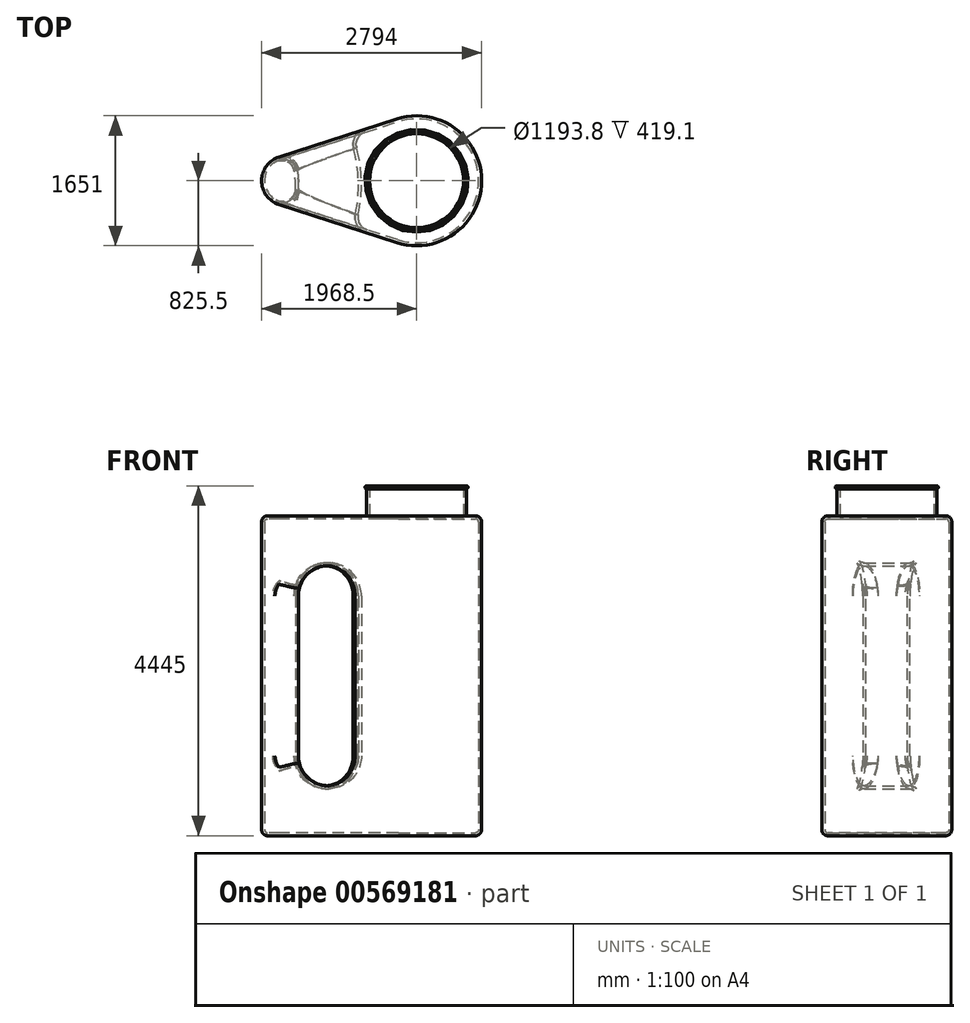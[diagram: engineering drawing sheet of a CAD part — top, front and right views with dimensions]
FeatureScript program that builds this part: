
annotation { "Feature Type Name" : "Feature", "Feature Type Description" : "" }
export const myFeature = defineFeature(function(context is Context, id is Id, definition is map)
    precondition{}
    {
        {
            var Q0;
            Q0=qCreatedBy(makeId("Top.planeOp"),FACE);
            var sketch = newSketch(context, id + "F0", { "sketchPlane" : qUnion([Q0])});
            skArc(sketch, "E0", {"start": v(-254, -785.45) * mm, "mid": v(825.5, 0) * mm, "end": v(-254, 785.45) * mm});
            skLineSegment(sketch, "E1", {"start": v(-254, 785.45) * mm, "end": v(-1748.7, 302.1) * mm});
            skLineSegment(sketch, "E2", {"start": v(-1748.7, -302.1) * mm, "end": v(-254, -785.45) * mm});
            skArc(sketch, "E3", {"start": v(-1748.7, 302.1) * mm, "mid": v(-1968.5, 0) * mm, "end": v(-1748.7, -302.1) * mm});
            skSolve(sketch);
        }
        {
            var Q0;
            Q0=makeQuery(id+"F0.imprint","IMPRINT",FACE,{"disambiguationData":[TD([[makeQuery(id+"F0.imprint","IMPRINT",EDGE,{"derivedFrom":sQuery(id+"F0.wireOp",EDGE,"E0")}),1.0]])]});
            extrude(context, id + "F1", {"entities" : qUnion([Q0]), "depth" : 4064 * mm, "offsetDistance" : 25.4 * mm});
        }
        {
            var Q0;
            Q0=makeQuery(id+"F1.opExtrude","SWEPT_FACE",FACE,{"disambiguationData":[OSD([sQuery(id+"F0.wireOp",EDGE,"E2")])]});
            var sketch = newSketch(context, id + "F2", { "sketchPlane" : qUnion([Q0])});
            skArc(sketch, "E4", {"start": v(-600.09, 3048) * mm, "mid": v(-981.09, 3429) * mm, "end": v(-1362.09, 3048) * mm});
            skArc(sketch, "E5", {"start": v(-1362.08, 1016) * mm, "mid": v(-981.08, 635) * mm, "end": v(-600.08, 1016) * mm});
            skLineSegment(sketch, "E6", {"start": v(-600.09, 3048) * mm, "end": v(-600.08, 1016) * mm});
            skLineSegment(sketch, "E7", {"start": v(-1362.09, 3048) * mm, "end": v(-1362.08, 1016) * mm});
            skLineSegment(sketch, "E8", {"start": v(-2387.75, 4364.56) * mm, "end": v(-2387.75, -220.57) * mm, "construction": true});
            skLineSegment(sketch, "E9", {"start": v(283.93, 0) * mm, "end": v(283.93, 5172.73) * mm, "construction": true});
            skSolve(sketch);
        }
        {
            var Q0;
            Q0=makeQuery(id+"F2.imprint","IMPRINT",FACE,{"disambiguationData":[TD([[makeQuery(id+"F2.imprint","IMPRINT",EDGE,{"derivedFrom":sQuery(id+"F2.wireOp",EDGE,"E4")}),1.0]])]});
            var Q1;
            Q1=sQuery(id+"F2.wireOp",EDGE,"E8");
            revolve(context, id + "F3", {"operationType" : NewBodyOperationType.REMOVE, "entities" : qUnion([Q0]), "axis" : qUnion([Q1]), "revolveType" : RevolveType.FULL, "oppositeDirection" : true});
        }
        {
            var Q0;
            Q0=makeQuery(id+"F1.opExtrude","CAP_FACE",FACE,{"disambiguationData":[OSD([sQuery(id+"F0.wireOp",EDGE,"E0"),sQuery(id+"F0.wireOp",EDGE,"E1"),sQuery(id+"F0.wireOp",EDGE,"E2"),sQuery(id+"F0.wireOp",EDGE,"E3")])],"isStart":false});
            var sketch = newSketch(context, id + "F4", { "sketchPlane" : qUnion([Q0])});
            skCircle(sketch, "E10", {"center": v(0, 0) * mm, "radius": 635 * mm});
            skSolve(sketch);
        }
        {
            var Q0;
            Q0=makeQuery(id+"F4.imprint","IMPRINT",FACE,{"disambiguationData":[TD([[makeQuery(id+"F4.imprint","IMPRINT",EDGE,{"derivedFrom":sQuery(id+"F4.wireOp",EDGE,"E10")}),1.0]])]});
            extrude(context, id + "F5", {"entities" : qUnion([Q0]), "operationType" : NewBodyOperationType.ADD, "depth" : 381 * mm, "offsetDistance" : 25.4 * mm});
        }
        {
            var Q0;
            Q0=makeQuery(id+"F3.boolean.opBoolean","INTERSECT",EDGE,{"derivedFrom":[makeQuery(id+"F1.opExtrude","SWEPT_FACE",FACE,{"disambiguationData":[OSD([sQuery(id+"F0.wireOp",EDGE,"E2")])]}),makeQuery(id+"F3.opRevolve","SWEPT_FACE",FACE,{"disambiguationData":[OSD([sQuery(id+"F2.wireOp",EDGE,"E7")])]})]});
            var Q1;
            Q1=makeQuery(id+"F3.boolean.opBoolean","INTERSECT",EDGE,{"derivedFrom":[makeQuery(id+"F1.opExtrude","SWEPT_FACE",FACE,{"disambiguationData":[OSD([sQuery(id+"F0.wireOp",EDGE,"E2")])]}),makeQuery(id+"F3.opRevolve","SWEPT_FACE",FACE,{"disambiguationData":[OSD([sQuery(id+"F2.wireOp",EDGE,"E4")])]})]});
            var Q2;
            Q2=makeQuery(id+"F3.boolean.opBoolean","INTERSECT",EDGE,{"derivedFrom":[makeQuery(id+"F1.opExtrude","SWEPT_FACE",FACE,{"disambiguationData":[OSD([sQuery(id+"F0.wireOp",EDGE,"E2")])]}),makeQuery(id+"F3.opRevolve","SWEPT_FACE",FACE,{"disambiguationData":[OSD([sQuery(id+"F2.wireOp",EDGE,"E6")])]})]});
            var Q3;
            Q3=makeQuery(id+"F3.boolean.opBoolean","INTERSECT",EDGE,{"derivedFrom":[makeQuery(id+"F1.opExtrude","SWEPT_FACE",FACE,{"disambiguationData":[OSD([sQuery(id+"F0.wireOp",EDGE,"E2")])]}),makeQuery(id+"F3.opRevolve","SWEPT_FACE",FACE,{"disambiguationData":[OSD([sQuery(id+"F2.wireOp",EDGE,"E5")])]})]});
            fillet(context, id + "F6", {"entities" : qUnion([Q0, Q1, Q2, Q3]), "radius" : 203.2 * mm, "tangentPropagation" : true, "allowEdgeOverflow" : false});
        }
        {
            var Q0;
            Q0=makeQuery(id+"F3.boolean.opBoolean","INTERSECT",EDGE,{"derivedFrom":[makeQuery(id+"F1.opExtrude","SWEPT_FACE",FACE,{"disambiguationData":[OSD([sQuery(id+"F0.wireOp",EDGE,"E1")])]}),makeQuery(id+"F3.opRevolve","SWEPT_FACE",FACE,{"disambiguationData":[OSD([sQuery(id+"F2.wireOp",EDGE,"E4")])]})]});
            var Q1;
            Q1=makeQuery(id+"F3.boolean.opBoolean","INTERSECT",EDGE,{"derivedFrom":[makeQuery(id+"F1.opExtrude","SWEPT_FACE",FACE,{"disambiguationData":[OSD([sQuery(id+"F0.wireOp",EDGE,"E1")])]}),makeQuery(id+"F3.opRevolve","SWEPT_FACE",FACE,{"disambiguationData":[OSD([sQuery(id+"F2.wireOp",EDGE,"E7")])]})]});
            var Q2;
            Q2=makeQuery(id+"F3.boolean.opBoolean","INTERSECT",EDGE,{"derivedFrom":[makeQuery(id+"F1.opExtrude","SWEPT_FACE",FACE,{"disambiguationData":[OSD([sQuery(id+"F0.wireOp",EDGE,"E1")])]}),makeQuery(id+"F3.opRevolve","SWEPT_FACE",FACE,{"disambiguationData":[OSD([sQuery(id+"F2.wireOp",EDGE,"E5")])]})]});
            var Q3;
            Q3=makeQuery(id+"F3.boolean.opBoolean","INTERSECT",EDGE,{"derivedFrom":[makeQuery(id+"F1.opExtrude","SWEPT_FACE",FACE,{"disambiguationData":[OSD([sQuery(id+"F0.wireOp",EDGE,"E1")])]}),makeQuery(id+"F3.opRevolve","SWEPT_FACE",FACE,{"disambiguationData":[OSD([sQuery(id+"F2.wireOp",EDGE,"E6")])]})]});
            fillet(context, id + "F7", {"entities" : qUnion([Q0, Q1, Q2, Q3]), "radius" : 203.2 * mm, "tangentPropagation" : true, "allowEdgeOverflow" : false});
        }
        {
            var Q0;
            Q0=makeQuery(id+"F1.opExtrude","CAP_EDGE",EDGE,{"disambiguationData":[OSD([sQuery(id+"F0.wireOp",EDGE,"E1")])],"isStart":false});
            var Q1;
            Q1=makeQuery(id+"F1.opExtrude","CAP_EDGE",EDGE,{"disambiguationData":[OSD([sQuery(id+"F0.wireOp",EDGE,"E3")])],"isStart":false});
            var Q2;
            Q2=makeQuery(id+"F1.opExtrude","CAP_EDGE",EDGE,{"disambiguationData":[OSD([sQuery(id+"F0.wireOp",EDGE,"E2")])],"isStart":false});
            var Q3;
            Q3=makeQuery(id+"F5.opExtrude","CAP_EDGE",EDGE,{"disambiguationData":[OSD([sQuery(id+"F4.wireOp",EDGE,"E10")])],"isStart":true});
            var Q4;
            Q4=makeQuery(id+"F1.opExtrude","CAP_EDGE",EDGE,{"disambiguationData":[OSD([sQuery(id+"F0.wireOp",EDGE,"E0")])],"isStart":false});
            fillet(context, id + "F8", {"entities" : qUnion([Q0, Q1, Q2, Q3, Q4]), "radius" : 76.2 * mm, "tangentPropagation" : true, "allowEdgeOverflow" : false});
        }
        {
            var Q0;
            Q0=makeQuery(id+"F1.opExtrude","CAP_FACE",FACE,{"disambiguationData":[OSD([sQuery(id+"F0.wireOp",EDGE,"E0"),sQuery(id+"F0.wireOp",EDGE,"E1"),sQuery(id+"F0.wireOp",EDGE,"E2"),sQuery(id+"F0.wireOp",EDGE,"E3")])],"isStart":true});
            fillet(context, id + "F9", {"entities" : qUnion([Q0]), "radius" : 76.2 * mm, "tangentPropagation" : true, "allowEdgeOverflow" : false});
        }
        {
            var Q0;
            Q0=makeQuery(id+"F5.opExtrude","CAP_FACE",FACE,{"disambiguationData":[OSD([sQuery(id+"F4.wireOp",EDGE,"E10")])],"isStart":false});
            shell(context, id + "F10", {"entities" : qUnion([Q0]), "thickness" : 38.1 * mm});
        }
        {
            var Q0;
            Q0=qCreatedBy(makeId("Front.planeOp"),FACE);
            var sketch = newSketch(context, id + "F11", { "sketchPlane" : qUnion([Q0])});
            skLineSegment(sketch, "E11", {"start": v(633.9, 4445.07) * mm, "end": v(633.9, 4137.62) * mm});
            skArc(sketch, "E12", {"start": v(633.9, 4406.9) * mm, "mid": v(652.96, 4425.95) * mm, "end": v(633.9, 4445) * mm});
            skLineSegment(sketch, "E13", {"start": v(-1.1, 4794.56) * mm, "end": v(-1.1, 4244.6) * mm, "construction": true});
            skSolve(sketch);
        }
        {
            var Q0;
            {var subQ0=sQuery(id+"F11.wireOp",EDGE,"E12");Q0=makeQuery(id+"F11.imprint","IMPRINT",FACE,{"disambiguationData":[TD([[makeQuery(id+"F11.imprint","IMPRINT",EDGE,{"derivedFrom":subQ0}),1.0]])]});}
            var Q1;
            Q1=sQuery(id+"F11.wireOp",EDGE,"E13");
            revolve(context, id + "F12", {"operationType" : NewBodyOperationType.ADD, "entities" : qUnion([Q0]), "axis" : qUnion([Q1]), "revolveType" : RevolveType.FULL});
        }
    });
